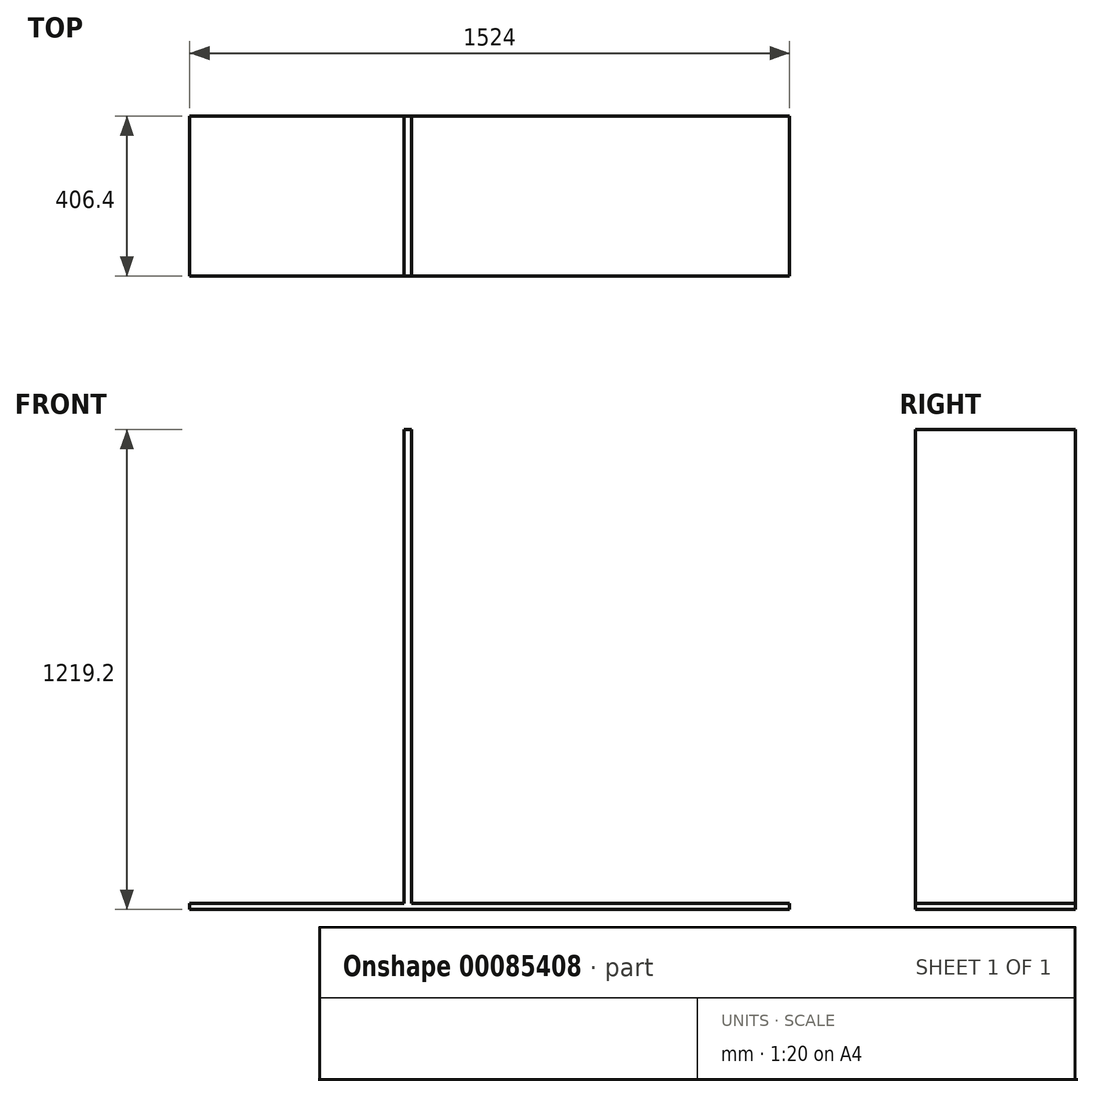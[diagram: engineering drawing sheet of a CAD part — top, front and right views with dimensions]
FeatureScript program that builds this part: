
annotation { "Feature Type Name" : "Feature", "Feature Type Description" : "" }
export const myFeature = defineFeature(function(context is Context, id is Id, definition is map)
    precondition{}
    {
        {
            var Q0;
            Q0=qCreatedBy(makeId("Right.planeOp"),FACE);
            var sketch = newSketch(context, id + "F0", { "sketchPlane" : qUnion([Q0])});
            skLineSegment(sketch, "E0.bottom", {"start": v(0, 0) * mm, "end": v(406.4, 0) * mm});
            skLineSegment(sketch, "E0.top", {"start": v(0, 15.87) * mm, "end": v(406.4, 15.87) * mm});
            skLineSegment(sketch, "E0.left", {"start": v(0, 0) * mm, "end": v(0, 15.87) * mm});
            skLineSegment(sketch, "E0.right", {"start": v(406.4, 0) * mm, "end": v(406.4, 15.87) * mm});
            skSolve(sketch);
        }
        {
            var Q0;
            Q0 = qSketchRegion(id + "F0", true);
            extrude(context, id + "F1", {"entities" : qUnion([Q0]), "depth" : 762 * mm});
        }
        {
            var Q0;
            Q0=makeQuery(id+"F1.opExtrude","SWEPT_BODY",BODY,{"disambiguationData":[OSD([sQuery(id+"F0.wireOp",EDGE,"E0.bottom"),sQuery(id+"F0.wireOp",EDGE,"E0.top"),sQuery(id+"F0.wireOp",EDGE,"E0.left"),sQuery(id+"F0.wireOp",EDGE,"E0.right")])]});
            var Q1;
            Q1=qCreatedBy(makeId("Right.planeOp"),FACE);
            mirror(context, id + "F2", {"operationType" : NewBodyOperationType.ADD, "entities" : qUnion([Q0]), "mirrorPlane" : qUnion([Q1])});
        }
        {
            var Q0;
            {var subQ0=makeQuery(id+"F1.opExtrude","SWEPT_FACE",FACE,{"disambiguationData":[OSD([sQuery(id+"F0.wireOp",EDGE,"E0.bottom")])]});Q0=makeQuery(id+"F2.boolean.opBoolean","MERGE",FACE,{"derivedFrom":[subQ0,makeQuery(id+"F2.opPattern","COPY",FACE,{"derivedFrom":subQ0,"instanceName":"1"})]});}
            var sketch = newSketch(context, id + "F3", { "sketchPlane" : qUnion([Q0])});
            skSolve(sketch);
        }
        {
            var Q0;
            {var subQ0=sQuery(id+"F0.wireOp",EDGE,"E0.bottom");var subQ1=makeQuery(id+"F1.opExtrude","CAP_EDGE",EDGE,{"disambiguationData":[OSD([subQ0])],"isStart":false});Q0=makeQuery(id+"F3.imprint","IMPRINT",FACE,{"disambiguationData":[TD([[makeQuery(id+"F3.imprint","IMPRINT",EDGE,{"derivedFrom":subQ1}),-1.0]])]});}
            var sketch = newSketch(context, id + "F4", { "sketchPlane" : qUnion([Q0])});
            skLineSegment(sketch, "E1.bottom", {"start": v(-199.26, 0) * mm, "end": v(-218.3, 0) * mm});
            skLineSegment(sketch, "E1.top", {"start": v(-199.26, -406.4) * mm, "end": v(-218.3, -406.4) * mm});
            skLineSegment(sketch, "E1.left", {"start": v(-199.26, 0) * mm, "end": v(-199.26, -406.4) * mm});
            skLineSegment(sketch, "E1.right", {"start": v(-218.3, 0) * mm, "end": v(-218.3, -406.4) * mm});
            skSolve(sketch);
        }
        {
            var Q0;
            {var subQ7=sQuery(id+"F4.wireOp",EDGE,"E1.top");Q0=makeQuery(id+"F4.imprint","IMPRINT",FACE,{"disambiguationData":[TD([[makeQuery(id+"F4.imprint","IMPRINT",EDGE,{"derivedFrom":subQ7}),-1.0]])]});}
            extrude(context, id + "F5", {"entities" : qUnion([Q0]), "operationType" : NewBodyOperationType.ADD, "oppositeDirection" : true, "depth" : 1219.2 * mm});
        }
    });
